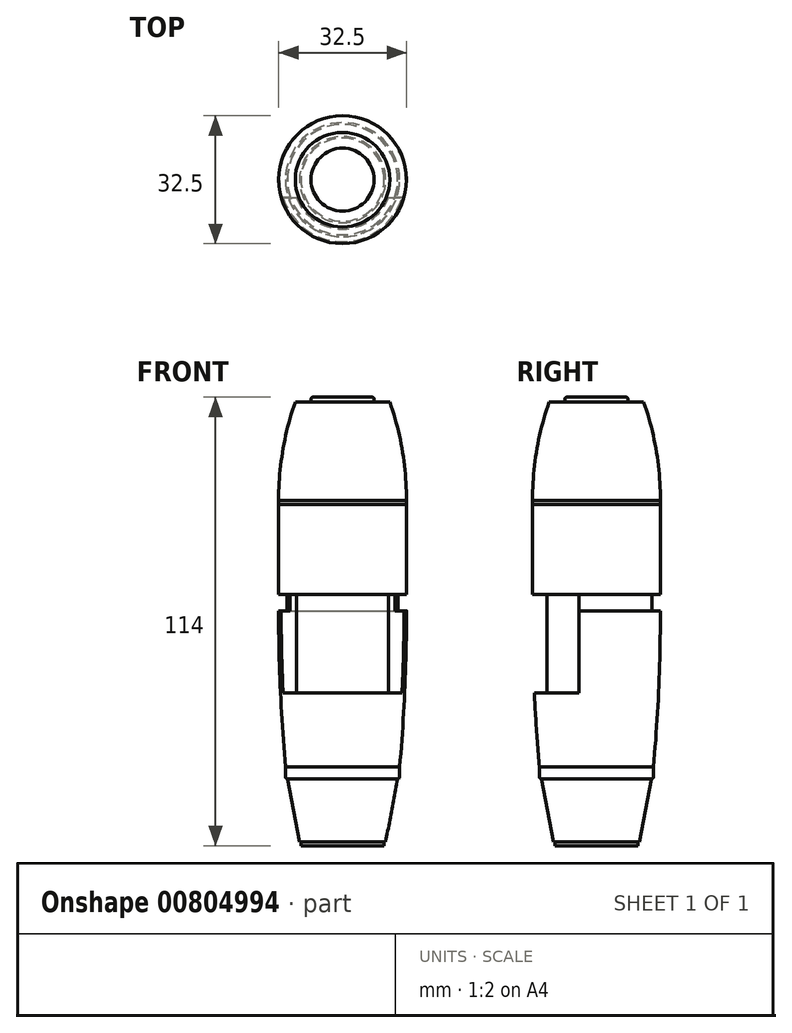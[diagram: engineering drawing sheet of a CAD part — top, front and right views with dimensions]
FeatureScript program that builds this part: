
annotation { "Feature Type Name" : "Feature", "Feature Type Description" : "" }
export const myFeature = defineFeature(function(context is Context, id is Id, definition is map)
    precondition{}
    {
        {
            var Q0;
            Q0=qCreatedBy(makeId("Front.planeOp"),FACE);
            var sketch = newSketch(context, id + "F0", { "sketchPlane" : qUnion([Q0])});
            skLineSegment(sketch, "E0", {"start": v(0, 0) * mm, "end": v(0, 94) * mm});
            skLineSegment(sketch, "E1", {"start": v(0, 94) * mm, "end": v(-8, 94) * mm});
            skLineSegment(sketch, "E2", {"start": v(-8, 94) * mm, "end": v(-8, 92.8) * mm});
            skLineSegment(sketch, "E3", {"start": v(-8, 92.8) * mm, "end": v(-12, 92.8) * mm});
            skArc(sketch, "E4", {"start": v(-12, 92.8) * mm, "mid": v(-15.18, 80.48) * mm, "end": v(-16.25, 67.8) * mm});
            skLineSegment(sketch, "E5", {"start": v(-16.25, 66.7) * mm, "end": v(-16.25, 43.8) * mm});
            skLineSegment(sketch, "E6", {"start": v(-16.25, 43.8) * mm, "end": v(-14.05, 43.8) * mm});
            skLineSegment(sketch, "E7", {"start": v(-14.05, 43.8) * mm, "end": v(-14.05, 39.7) * mm});
            skLineSegment(sketch, "E8", {"start": v(-14.05, 39.7) * mm, "end": v(-16.25, 39.7) * mm});
            skLineSegment(sketch, "E9", {"start": v(-14.5, 0) * mm, "end": v(0, 0) * mm});
            skLineSegment(sketch, "E10", {"start": v(-16.25, 67.8) * mm, "end": v(-16.05, 67.8) * mm});
            skLineSegment(sketch, "E11", {"start": v(-16.05, 67.8) * mm, "end": v(-16.05, 67.75) * mm});
            skLineSegment(sketch, "E12", {"start": v(-16.05, 67.75) * mm, "end": v(-16.25, 67.75) * mm});
            skLineSegment(sketch, "E13", {"start": v(-16.25, 67.75) * mm, "end": v(-16.25, 66.75) * mm});
            skLineSegment(sketch, "E14", {"start": v(-16.25, 66.75) * mm, "end": v(-16.05, 66.75) * mm});
            skLineSegment(sketch, "E15", {"start": v(-16.05, 66.75) * mm, "end": v(-16.05, 66.7) * mm});
            skLineSegment(sketch, "E16", {"start": v(-16.05, 66.7) * mm, "end": v(-16.25, 66.7) * mm});
            skArc(sketch, "E17", {"start": v(-16.25, 39.7) * mm, "mid": v(-15.81, 19.83) * mm, "end": v(-14.5, 0) * mm});
            skSolve(sketch);
        }
        {
            var Q0;
            Q0=makeQuery(id+"F0.imprint","IMPRINT",FACE,{"disambiguationData":[TD([[makeQuery(id+"F0.imprint","IMPRINT",EDGE,{"derivedFrom":sQuery(id+"F0.wireOp",EDGE,"E0")}),1.0]])]});
            var Q1;
            Q1=sQuery(id+"F0.wireOp",EDGE,"E4");
            var Q2;
            Q2=sQuery(id+"F0.wireOp",EDGE,"E3");
            var Q3;
            Q3=sQuery(id+"F0.wireOp",EDGE,"E2");
            var Q4;
            Q4=sQuery(id+"F0.wireOp",EDGE,"E1");
            var Q5;
            Q5=sQuery(id+"F0.wireOp",EDGE,"E0");
            revolve(context, id + "F1", {"surfaceOperationType" : NewSurfaceOperationType.NEW, "entities" : qUnion([Q0]), "surfaceEntities" : qUnion([Q1, Q2, Q3, Q4]), "axis" : qUnion([Q5]), "revolveType" : RevolveType.FULL});
        }
        {
            var Q0;
            Q0=makeQuery(id+"F1.opRevolve","SWEPT_FACE",FACE,{"disambiguationData":[OSD([sQuery(id+"F0.wireOp",EDGE,"E6")])]});
            var sketch = newSketch(context, id + "F2", { "sketchPlane" : qUnion([Q0])});
            skArc(sketch, "E18.0", {"start": v(15.61, 4.5) * mm, "mid": v(0, 16.25) * mm, "end": v(-15.61, 4.5) * mm});
            skArc(sketch, "E19", {"start": v(11.72, 4.5) * mm, "mid": v(0, 12.55) * mm, "end": v(-11.72, 4.5) * mm});
            skLineSegment(sketch, "E20", {"start": v(-15.61, 4.5) * mm, "end": v(-11.72, 4.5) * mm});
            skLineSegment(sketch, "E21", {"start": v(0, 14.5) * mm, "end": v(0, 4.5) * mm, "construction": true});
            skLineSegment(sketch, "E22.trimOffspring", {"start": v(11.72, 4.5) * mm, "end": v(15.61, 4.5) * mm});
            skSolve(sketch);
        }
        {
            var Q0;
            Q0 = qSketchRegion(id + "F2", true);
            extrude(context, id + "F3", {"entities" : qUnion([Q0]), "operationType" : NewBodyOperationType.REMOVE, "depth" : 25 * mm, "offsetDistance" : 25 * mm});
        }
        {
            var Q0;
            Q0=makeQuery(id+"F1.opRevolve","SWEPT_EDGE",EDGE,{"disambiguationData":[OSD([sQuery(id+"F0.wireOp",EDGE,"E1"),sQuery(id+"F0.wireOp",EDGE,"E2")])]});
            fillet(context, id + "F4", {"entities" : qUnion([Q0]), "radius" : 0.5 * mm, "tangentPropagation" : true, "allowEdgeOverflow" : false});
        }
        {
            var Q0;
            Q0=qCreatedBy(makeId("Front.planeOp"),FACE);
            var sketch = newSketch(context, id + "F5", { "sketchPlane" : qUnion([Q0])});
            skLineSegment(sketch, "E23", {"start": v(0, 0) * mm, "end": v(0, -20) * mm});
            skLineSegment(sketch, "E24", {"start": v(0, -20) * mm, "end": v(10.55, -20) * mm});
            skLineSegment(sketch, "E25", {"start": v(10.55, -19) * mm, "end": v(10.55, -20) * mm});
            skLineSegment(sketch, "E26", {"start": v(10.55, -19) * mm, "end": v(10.95, -19) * mm});
            skLineSegment(sketch, "E27", {"start": v(10.95, -19) * mm, "end": v(14, -3) * mm});
            skLineSegment(sketch, "E28", {"start": v(14, -3) * mm, "end": v(14.5, -3) * mm});
            skLineSegment(sketch, "E29", {"start": v(14.5, -3) * mm, "end": v(14.5, 0) * mm});
            skLineSegment(sketch, "E30", {"start": v(14.5, 0) * mm, "end": v(0, 0) * mm});
            skSolve(sketch);
        }
        {
            var Q0;
            Q0 = qSketchRegion(id + "F5", true);
            var Q1;
            Q1=sQuery(id+"F5.wireOp",EDGE,"E23");
            revolve(context, id + "F6", {"operationType" : NewBodyOperationType.ADD, "surfaceOperationType" : NewSurfaceOperationType.NEW, "entities" : qUnion([Q0]), "axis" : qUnion([Q1]), "revolveType" : RevolveType.FULL});
        }
        {
            var Q0;
            Q0=makeQuery(id+"F6.opRevolve","SWEPT_EDGE",EDGE,{"disambiguationData":[OSD([sQuery(id+"F5.wireOp",EDGE,"E28"),sQuery(id+"F5.wireOp",EDGE,"E29")])]});
            fillet(context, id + "F7", {"entities" : qUnion([Q0]), "radius" : .5 * mm, "tangentPropagation" : true, "allowEdgeOverflow" : false});
        }
    });
